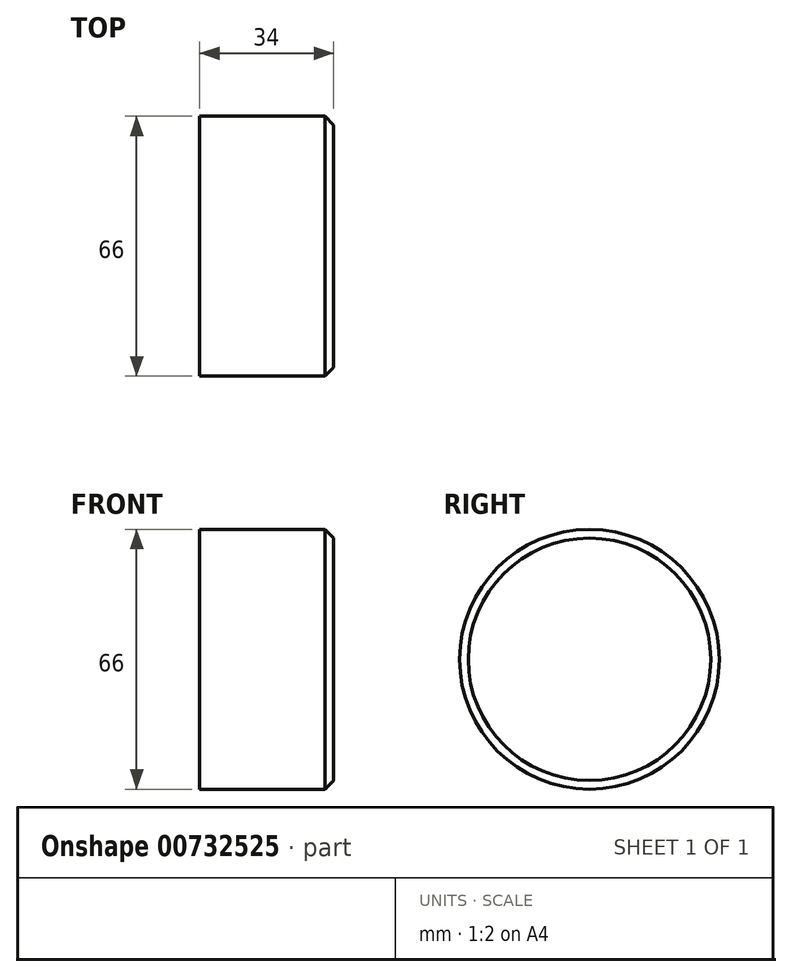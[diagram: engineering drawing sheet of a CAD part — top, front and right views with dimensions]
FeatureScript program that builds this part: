
annotation { "Feature Type Name" : "Feature", "Feature Type Description" : "" }
export const myFeature = defineFeature(function(context is Context, id is Id, definition is map)
    precondition{}
    {
        {
            var Q0;
            Q0=qCreatedBy(makeId("Right.planeOp"),FACE);
            var sketch = newSketch(context, id + "F0", { "sketchPlane" : qUnion([Q0])});
            skCircle(sketch, "E0", {"center": v(0, 0) * mm, "radius": 33 * mm});
            skSolve(sketch);
        }
        {
            var Q0;
            Q0 = qSketchRegion(id + "F0", true);
            extrude(context, id + "F1", {"entities" : qUnion([Q0]), "depth" : 9 * mm, "offsetDistance" : 25 * mm});
        }
        {
            var Q0;
            Q0=makeQuery(id+"F1.opExtrude","CAP_FACE",FACE,{"disambiguationData":[OSD([sQuery(id+"F0.wireOp",EDGE,"E0")])],"isStart":false});
            chamfer(context, id + "F2", {"entities" : qUnion([Q0]), "width" : 2.2 * mm, "tangentPropagation" : true});
        }
        {
            var Q0;
            Q0=makeQuery(id+"F1.opExtrude","CAP_FACE",FACE,{"disambiguationData":[OSD([sQuery(id+"F0.wireOp",EDGE,"E0")])],"isStart":true});
            extrude(context, id + "F3", {"entities" : qUnion([Q0]), "operationType" : NewBodyOperationType.ADD, "depth" : 25 * mm, "offsetDistance" : 25 * mm});
        }
    });
